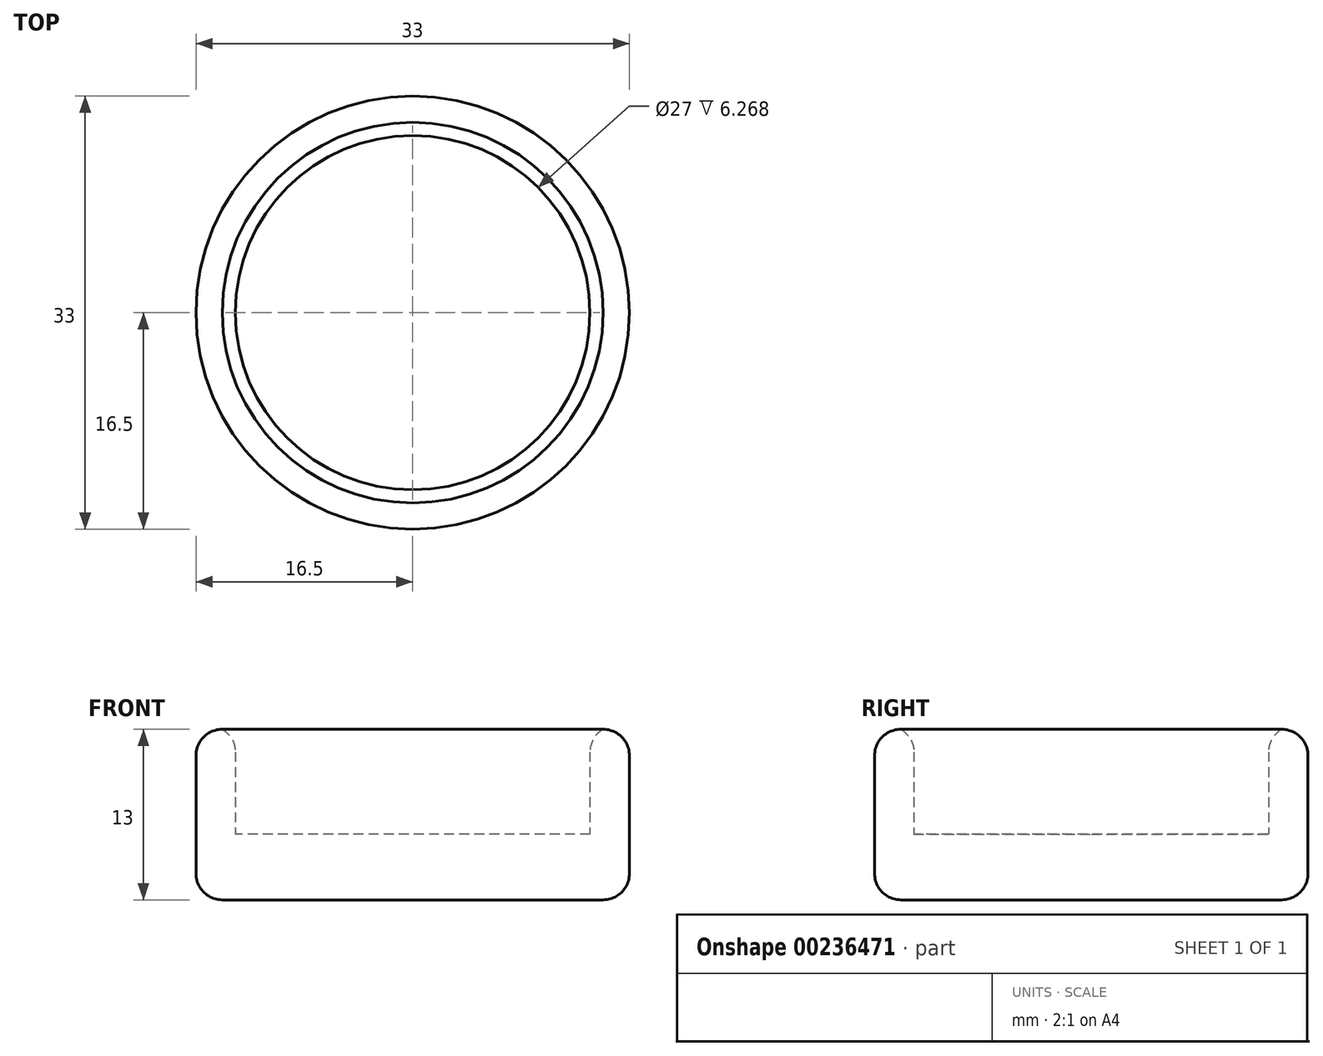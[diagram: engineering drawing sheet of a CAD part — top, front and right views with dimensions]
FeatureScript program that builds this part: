
annotation { "Feature Type Name" : "Feature", "Feature Type Description" : "" }
export const myFeature = defineFeature(function(context is Context, id is Id, definition is map)
    precondition{}
    {
        {
            var Q0;
            Q0=qCreatedBy(makeId("Top.planeOp"),FACE);
            var sketch = newSketch(context, id + "F0", { "sketchPlane" : qUnion([Q0])});
            skCircle(sketch, "E0", {"center": v(0, 0) * mm, "radius": 13.5 * mm});
            skCircle(sketch, "E1", {"center": v(0, 0) * mm, "radius": 16.5 * mm});
            skSolve(sketch);
        }
        {
            var Q0;
            Q0=makeQuery(id+"F0.imprint","IMPRINT",FACE,{"disambiguationData":[TD([[makeQuery(id+"F0.imprint","IMPRINT",EDGE,{"derivedFrom":sQuery(id+"F0.wireOp",EDGE,"E0")}),1.0]])]});
            extrude(context, id + "F1", {"entities" : qUnion([Q0]), "depth" : 5 * mm, "offsetDistance" : 25 * mm});
        }
        {
            var Q0;
            Q0 = qSketchRegion(id + "F0", true);
            extrude(context, id + "F2", {"entities" : qUnion([Q0]), "operationType" : NewBodyOperationType.ADD, "depth" : 13 * mm, "offsetDistance" : 25 * mm});
        }
        {
            var Q0;
            Q0=makeQuery(id+"F2.opExtrude","CAP_EDGE",EDGE,{"disambiguationData":[OSD([sQuery(id+"F0.wireOp",EDGE,"E1")])],"isStart":false});
            var Q1;
            Q1=makeQuery(id+"F2.opExtrude","CAP_EDGE",EDGE,{"disambiguationData":[OSD([sQuery(id+"F0.wireOp",EDGE,"E1")])],"isStart":true});
            fillet(context, id + "F3", {"entities" : qUnion([Q0, Q1]), "tangentPropagation" : true, "radius" : 2 * mm, "defaultsChanged" : true, "vertexSettings" : [], "allowEdgeOverflow" : false});
        }
        {
            var Q0;
            Q0=makeQuery(id+"F2.opExtrude","CAP_EDGE",EDGE,{"disambiguationData":[OSD([sQuery(id+"F0.wireOp",EDGE,"E0")])],"isStart":false});
            fillet(context, id + "F4", {"entities" : qUnion([Q0]), "tangentPropagation" : true, "radius" : 2 * mm, "defaultsChanged" : true, "vertexSettings" : [], "allowEdgeOverflow" : false});
        }
        {
            var Q0;
            Q0=makeQuery(id+"F1.opExtrude","SWEPT_BODY",BODY,{"disambiguationData":[OSD([sQuery(id+"F0.wireOp",EDGE,"E0")])]});
            transform(context, id + "F5", {"entities" : qUnion([Q0]), "transformType" : TransformType.TRANSLATION_3D, "dx" : 0 * mm, "dy" : 0 * mm, "dz" : 0 * mm, "makeCopy" : true});
        }
        {
            var Q0;
            Q0=makeQuery(id+"F5.opPattern","COPY",BODY,{"derivedFrom":makeQuery(id+"F1.opExtrude","SWEPT_BODY",BODY,{"disambiguationData":[OSD([sQuery(id+"F0.wireOp",EDGE,"E0")])]}),"instanceName":"1"});
            deleteBodies(context, id + "F6", {"entities" : qUnion([Q0])});
        }
        {
            var Q0;
            Q0=makeQuery(id+"F1.opExtrude","SWEPT_BODY",BODY,{"disambiguationData":[OSD([sQuery(id+"F0.wireOp",EDGE,"E0")])]});
            transform(context, id + "F7", {"entities" : qUnion([Q0]), "transformType" : TransformType.TRANSLATION_3D, "dx" : 0 * mm, "dy" : 36 * mm, "dz" : 0 * mm, "makeCopy" : true});
        }
        {
            var Q0;
            Q0=makeQuery(id+"F1.opExtrude","SWEPT_BODY",BODY,{"disambiguationData":[OSD([sQuery(id+"F0.wireOp",EDGE,"E0")])]});
            transform(context, id + "F8", {"entities" : qUnion([Q0]), "transformType" : TransformType.TRANSLATION_3D, "dx" : 36.3 * mm, "dy" : 0 * mm, "dz" : 0 * mm, "makeCopy" : true});
        }
        {
            var Q0;
            Q0=makeQuery(id+"F8.opPattern","COPY",BODY,{"derivedFrom":makeQuery(id+"F1.opExtrude","SWEPT_BODY",BODY,{"disambiguationData":[OSD([sQuery(id+"F0.wireOp",EDGE,"E0")])]}),"instanceName":"1"});
            transform(context, id + "F9", {"entities" : qUnion([Q0]), "transformType" : TransformType.TRANSLATION_3D, "dx" : -0.4 * mm, "dy" : 35.2 * mm, "dz" : 0 * mm, "makeCopy" : true});
        }
        {
            var Q0;
            Q0=makeQuery(id+"F7.opPattern","COPY",BODY,{"derivedFrom":makeQuery(id+"F1.opExtrude","SWEPT_BODY",BODY,{"disambiguationData":[OSD([sQuery(id+"F0.wireOp",EDGE,"E0")])]}),"instanceName":"1"});
            var Q1;
            Q1=makeQuery(id+"F8.opPattern","COPY",BODY,{"derivedFrom":makeQuery(id+"F1.opExtrude","SWEPT_BODY",BODY,{"disambiguationData":[OSD([sQuery(id+"F0.wireOp",EDGE,"E0")])]}),"instanceName":"1"});
            var Q2;
            Q2=makeQuery(id+"F9.opPattern","COPY",BODY,{"derivedFrom":makeQuery(id+"F8.opPattern","COPY",BODY,{"derivedFrom":makeQuery(id+"F1.opExtrude","SWEPT_BODY",BODY,{"disambiguationData":[OSD([sQuery(id+"F0.wireOp",EDGE,"E0")])]}),"instanceName":"1"}),"instanceName":"1"});
            deleteBodies(context, id + "F10", {"entities" : qUnion([Q0, Q1, Q2])});
        }
    });
